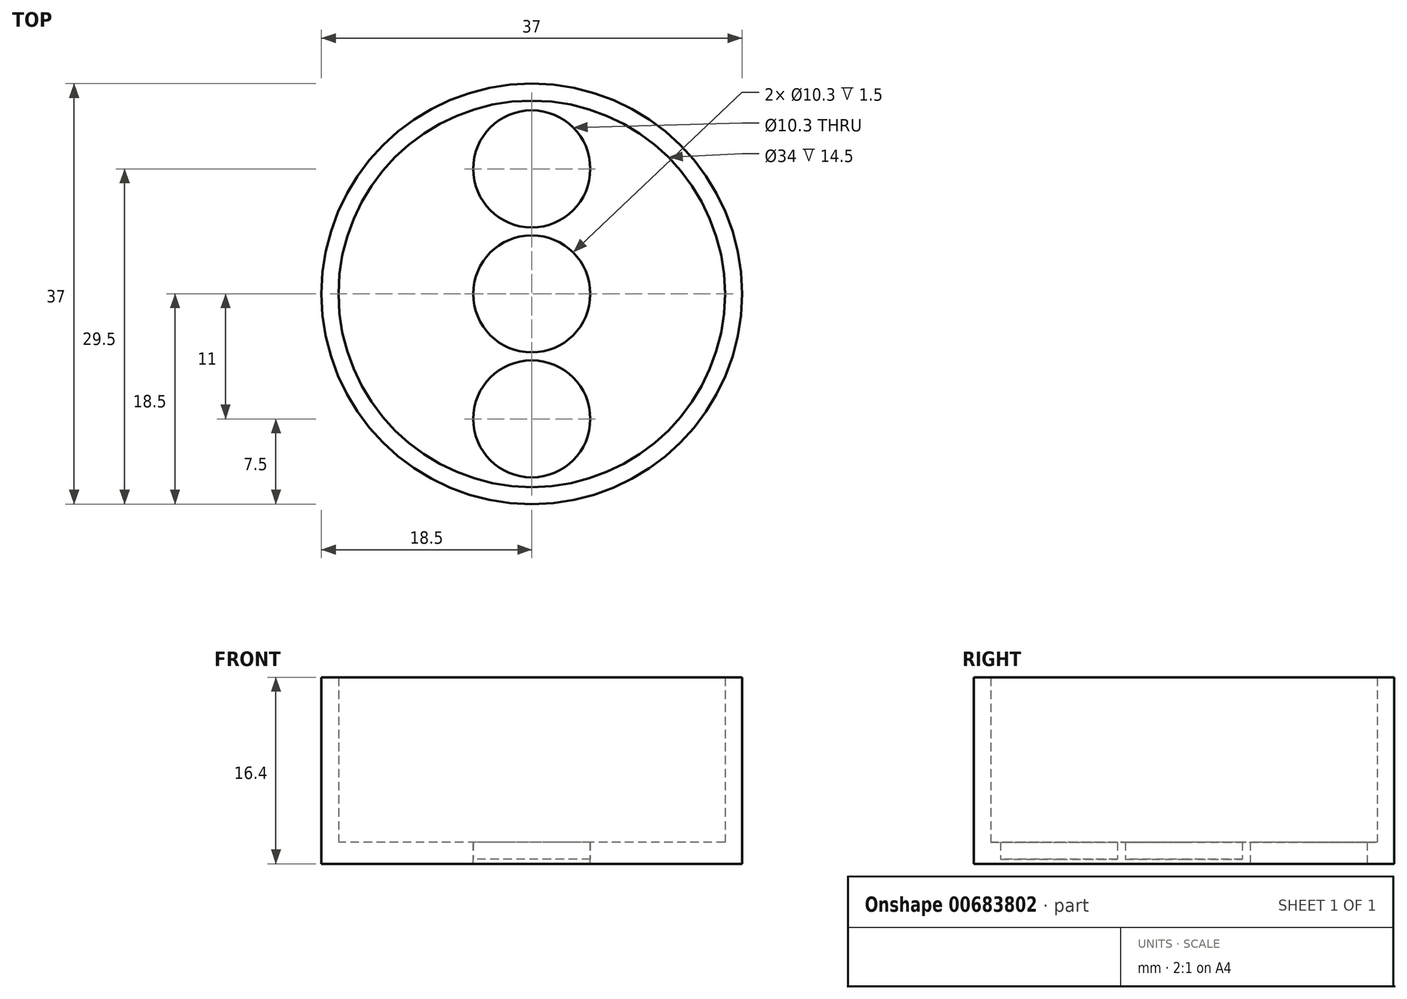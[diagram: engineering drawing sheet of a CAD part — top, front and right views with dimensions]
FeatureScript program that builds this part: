
annotation { "Feature Type Name" : "Feature", "Feature Type Description" : "" }
export const myFeature = defineFeature(function(context is Context, id is Id, definition is map)
    precondition{}
    {
        {
            assignVariable(context, id + "F0", {"name" : "btWandStaerke", "anyValue" : 1.5 * mm});
        }
        {
            assignVariable(context, id + "F1", {"name" : "folienStaerke", "anyValue" : 0.4 * mm});
        }
        {
            var Q0;
            Q0=qCreatedBy(makeId("Top.planeOp"),FACE);
            var sketch = newSketch(context, id + "F2", { "sketchPlane" : qUnion([Q0])});
            skCircle(sketch, "E0", {"center": v(0, 0) * mm, "radius": 5.15 * mm});
            skCircle(sketch, "E1", {"center": v(0, 0) * mm, "radius": 17 * mm});
            skCircle(sketch, "E2", {"center": v(0, 11) * mm, "radius": 5.15 * mm});
            skCircle(sketch, "E3", {"center": v(0, 0) * mm, "radius": 18.5 * mm});
            skCircle(sketch, "E4", {"center": v(0, -11) * mm, "radius": 5.15 * mm});
            skSolve(sketch);
        }
        {
            var Q0;
            Q0=makeQuery(id+"F2.imprint","IMPRINT",FACE,{"disambiguationData":[TD([[makeQuery(id+"F2.imprint","IMPRINT",EDGE,{"derivedFrom":sQuery(id+"F2.wireOp",EDGE,"E0")}),-1.0]])]});
            var Q1;
            Q1=makeQuery(id+"F2.imprint","IMPRINT",FACE,{"disambiguationData":[TD([[makeQuery(id+"F2.imprint","IMPRINT",EDGE,{"derivedFrom":sQuery(id+"F2.wireOp",EDGE,"E0")}),1.0]])]});
            var Q2;
            Q2=makeQuery(id+"F2.imprint","IMPRINT",FACE,{"disambiguationData":[TD([[makeQuery(id+"F2.imprint","IMPRINT",EDGE,{"derivedFrom":sQuery(id+"F2.wireOp",EDGE,"E4")}),1.0]])]});
            var Q3;
            Q3=makeQuery(id+"F2.imprint","IMPRINT",FACE,{"disambiguationData":[TD([[makeQuery(id+"F2.imprint","IMPRINT",EDGE,{"derivedFrom":sQuery(id+"F2.wireOp",EDGE,"E1")}),-1.0]])]});
            extrude(context, id + "F3", {"entities" : qUnion([Q0, Q1, Q2, Q3]), "oppositeDirection" : true, "depth" : getVariable(context, 'folienStaerke'), "offsetDistance" : 25 * mm});
        }
        {
            var Q0;
            Q0=makeQuery(id+"F2.imprint","IMPRINT",FACE,{"disambiguationData":[TD([[makeQuery(id+"F2.imprint","IMPRINT",EDGE,{"derivedFrom":sQuery(id+"F2.wireOp",EDGE,"E0")}),-1.0]])]});
            extrude(context, id + "F4", {"entities" : qUnion([Q0]), "operationType" : NewBodyOperationType.ADD, "depth" : getVariable(context, 'btWandStaerke'), "offsetDistance" : 25 * mm});
        }
        {
            var Q0;
            Q0=makeQuery(id+"F2.imprint","IMPRINT",FACE,{"disambiguationData":[TD([[makeQuery(id+"F2.imprint","IMPRINT",EDGE,{"derivedFrom":sQuery(id+"F2.wireOp",EDGE,"E1")}),-1.0]])]});
            extrude(context, id + "F5", {"entities" : qUnion([Q0]), "operationType" : NewBodyOperationType.ADD, "depth" : 16 * mm, "offsetDistance" : 25 * mm});
        }
    });
